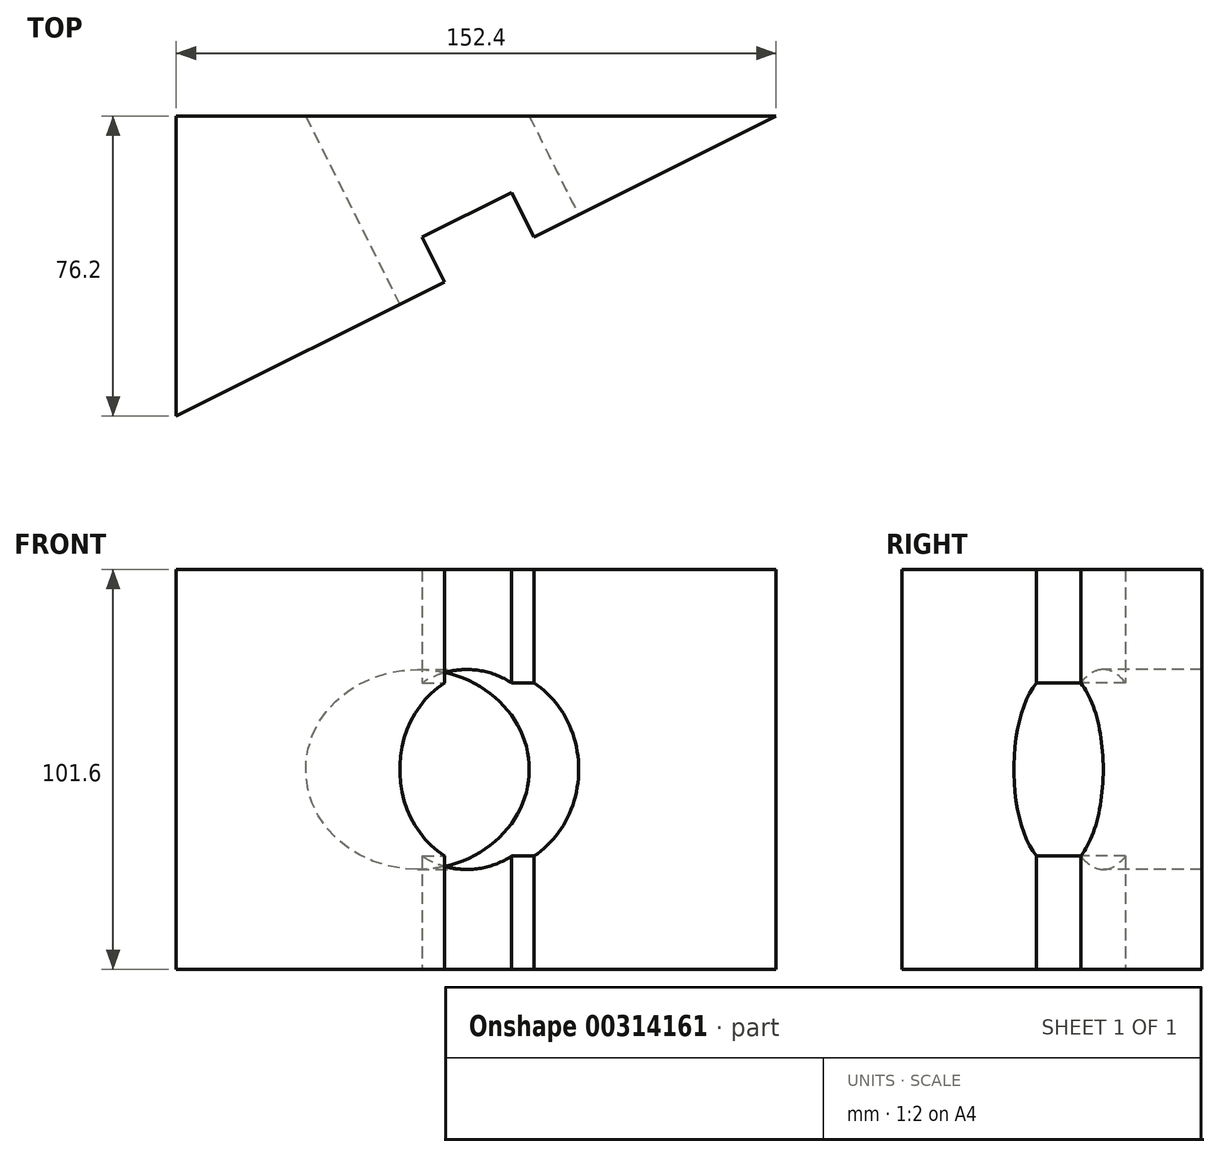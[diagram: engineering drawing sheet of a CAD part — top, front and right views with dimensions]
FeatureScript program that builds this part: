
annotation { "Feature Type Name" : "Feature", "Feature Type Description" : "" }
export const myFeature = defineFeature(function(context is Context, id is Id, definition is map)
    precondition{}
    {
        {
            var Q0;
            Q0=qCreatedBy(makeId("Top.planeOp"),FACE);
            var sketch = newSketch(context, id + "F0", { "sketchPlane" : qUnion([Q0])});
            skLineSegment(sketch, "E0.bottom", {"start": v(0, 0) * mm, "end": v(152.4, 0) * mm});
            skLineSegment(sketch, "E0.top", {"start": v(0, -76.2) * mm, "end": v(152.4, -76.2) * mm});
            skLineSegment(sketch, "E0.left", {"start": v(0, 0) * mm, "end": v(0, -76.2) * mm});
            skLineSegment(sketch, "E0.right", {"start": v(152.4, 0) * mm, "end": v(152.4, -76.2) * mm});
            skLineSegment(sketch, "E1", {"start": v(0, -76.2) * mm, "end": v(152.4, 0) * mm});
            skSolve(sketch);
        }
        {
            var Q0;
            Q0=makeQuery(id+"F0.imprint","IMPRINT",FACE,{"disambiguationData":[TD([[makeQuery(id+"F0.imprint","IMPRINT",EDGE,{"derivedFrom":sQuery(id+"F0.wireOp",EDGE,"E0.bottom")}),-1.0]])]});
            var Q1;
            Q1 = qSketchRegion(id + "F2", true);
            extrude(context, id + "F1", {"entities" : qUnion([Q0, Q1]), "depth" : 101.6 * mm});
        }
        {
            var Q0;
            Q0=makeQuery(id+"F1.opExtrude","SWEPT_FACE",FACE,{"disambiguationData":[OSD([sQuery(id+"F0.wireOp",EDGE,"E1")])]});
            var sketch = newSketch(context, id + "F2", { "sketchPlane" : qUnion([Q0])});
            skLineSegment(sketch, "E2.bottom", {"start": v(42.12, 101.6) * mm, "end": v(67.52, 101.6) * mm});
            skLineSegment(sketch, "E2.top", {"start": v(42.12, 0) * mm, "end": v(67.52, 0) * mm});
            skLineSegment(sketch, "E2.left", {"start": v(42.12, 101.6) * mm, "end": v(42.12, 0) * mm});
            skLineSegment(sketch, "E2.right", {"start": v(67.52, 101.6) * mm, "end": v(67.52, 0) * mm});
            skPoint(sketch, "E2.middle", {"position": v(54.82, 50.8) * mm});
            skSolve(sketch);
        }
        {
            var Q0;
            Q0=makeQuery(id+"F2.imprint","IMPRINT",FACE,{"disambiguationData":[TD([[makeQuery(id+"F2.imprint","IMPRINT",EDGE,{"derivedFrom":sQuery(id+"F2.wireOp",EDGE,"E2.bottom")}),-1.0]])]});
            extrude(context, id + "F3", {"entities" : qUnion([Q0]), "operationType" : NewBodyOperationType.REMOVE, "oppositeDirection" : true, "depth" : 12.7 * mm});
        }
        {
            var Q0;
            {var subQ0=sQuery(id+"F2.wireOp",EDGE,"E2.left");Q0=makeQuery(id+"F2.imprint","IMPRINT",FACE,{"disambiguationData":[TD([[makeQuery(id+"F2.imprint","IMPRINT",EDGE,{"derivedFrom":subQ0}),-1.0]])]});}
            var sketch = newSketch(context, id + "F4", { "sketchPlane" : qUnion([Q0])});
            skCircle(sketch, "E3", {"center": v(54.82, 50.8) * mm, "radius": 25.4 * mm});
            skSolve(sketch);
        }
        {
            var Q0;
            Q0 = qSketchRegion(id + "F4", true);
            extrude(context, id + "F5", {"entities" : qUnion([Q0]), "operationType" : NewBodyOperationType.REMOVE, "endBound" : BoundingType.THROUGH_ALL, "oppositeDirection" : true, "depth" : 25.4 * mm});
        }
    });
